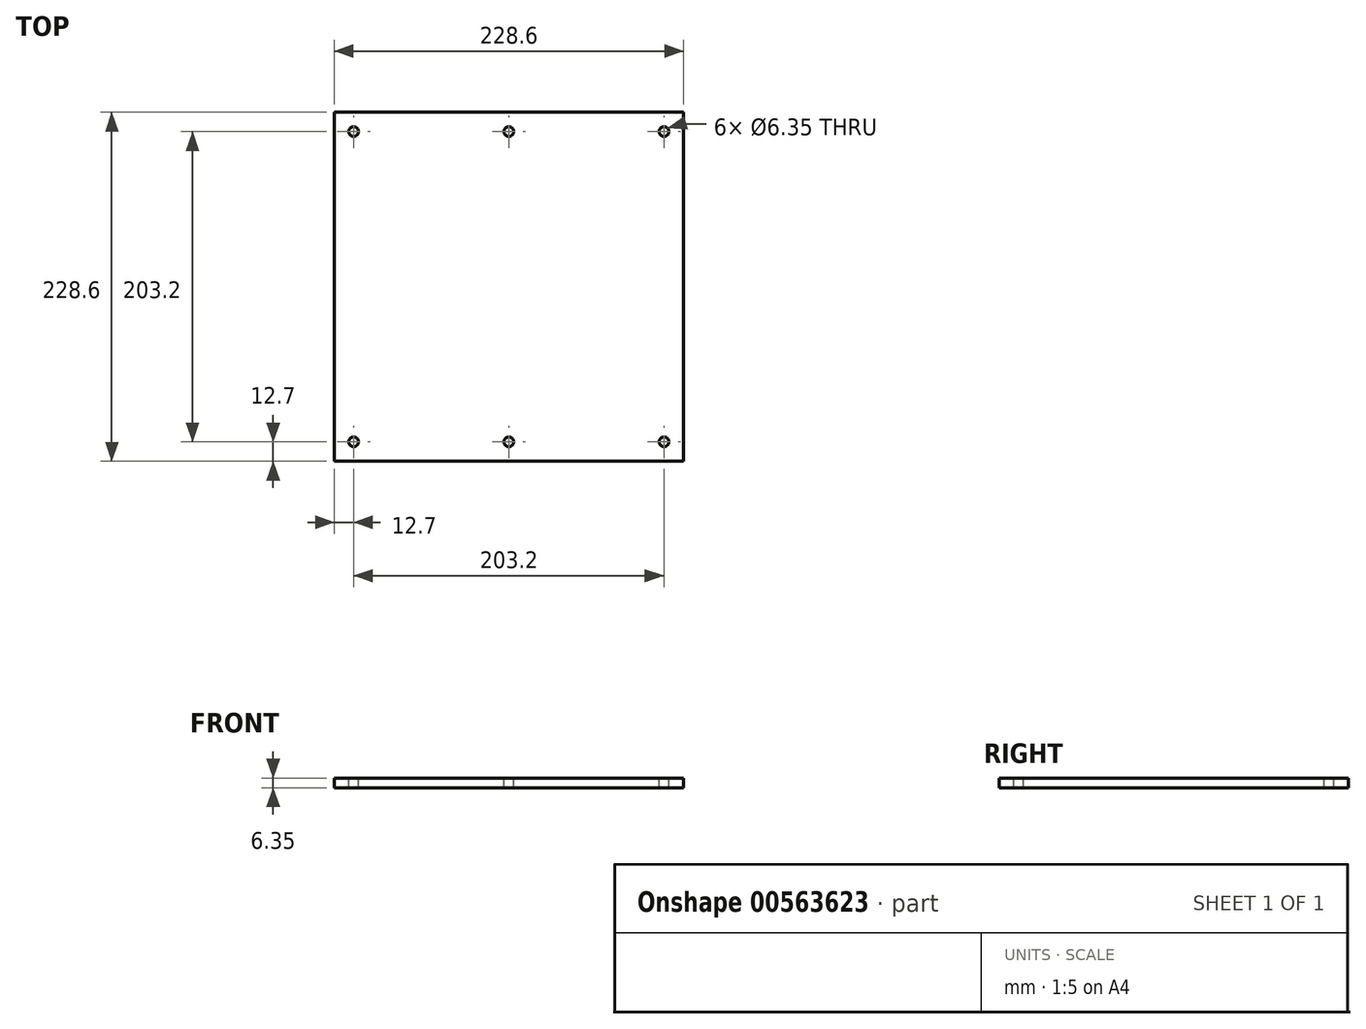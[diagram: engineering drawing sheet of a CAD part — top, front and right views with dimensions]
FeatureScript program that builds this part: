
annotation { "Feature Type Name" : "Feature", "Feature Type Description" : "" }
export const myFeature = defineFeature(function(context is Context, id is Id, definition is map)
    precondition{}
    {
        {
            var Q0;
            Q0=qCreatedBy(makeId("Top.planeOp"),FACE);
            var sketch = newSketch(context, id + "F0", { "sketchPlane" : qUnion([Q0])});
            skLineSegment(sketch, "E0.bottom", {"start": v(0, 0) * mm, "end": v(228.6, 0) * mm});
            skLineSegment(sketch, "E0.top", {"start": v(0, 228.6) * mm, "end": v(228.6, 228.6) * mm});
            skLineSegment(sketch, "E0.left", {"start": v(0, 0) * mm, "end": v(0, 228.6) * mm});
            skLineSegment(sketch, "E0.right", {"start": v(228.6, 0) * mm, "end": v(228.6, 228.6) * mm});
            skSolve(sketch);
        }
        {
            var Q0;
            Q0 = qSketchRegion(id + "F0", true);
            extrude(context, id + "F1", {"entities" : qUnion([Q0]), "depth" : 6.35 * mm, "offsetDistance" : 25.4 * mm});
        }
        {
            var Q0;
            Q0=makeQuery(id+"F1.opExtrude","CAP_FACE",FACE,{"disambiguationData":[OSD([sQuery(id+"F0.wireOp",EDGE,"E0.bottom"),sQuery(id+"F0.wireOp",EDGE,"E0.top"),sQuery(id+"F0.wireOp",EDGE,"E0.left"),sQuery(id+"F0.wireOp",EDGE,"E0.right")])],"isStart":false});
            var sketch = newSketch(context, id + "F2", { "sketchPlane" : qUnion([Q0])});
            skLineSegment(sketch, "E1", {"start": v(0, 114.3) * mm, "end": v(228.6, 114.3) * mm});
            skLineSegment(sketch, "E2", {"start": v(0, 12.7) * mm, "end": v(228.6, 12.7) * mm});
            skCircle(sketch, "E3", {"center": v(12.7, 12.7) * mm, "radius": 3.18 * mm});
            skLineSegment(sketch, "E4", {"start": v(114.3, 228.6) * mm, "end": v(114.3, 0) * mm});
            skCircle(sketch, "E5", {"center": v(114.3, 12.7) * mm, "radius": 3.18 * mm});
            skCircle(sketch, "E6.MirrorC", {"center": v(215.9, 12.7) * mm, "radius": 3.18 * mm});
            skCircle(sketch, "E7.MirrorC", {"center": v(12.7, 215.9) * mm, "radius": 3.18 * mm});
            skCircle(sketch, "E8.MirrorC", {"center": v(114.3, 215.9) * mm, "radius": 3.18 * mm});
            skCircle(sketch, "E9.MirrorC", {"center": v(215.9, 215.9) * mm, "radius": 3.18 * mm});
            skSolve(sketch);
        }
        {
            var Q0;
            Q0 = qSketchRegion(id + "F2", true);
            extrude(context, id + "F3", {"entities" : qUnion([Q0]), "operationType" : NewBodyOperationType.REMOVE, "oppositeDirection" : true, "depth" : 25.4 * mm, "offsetDistance" : 25.4 * mm});
        }
    });
